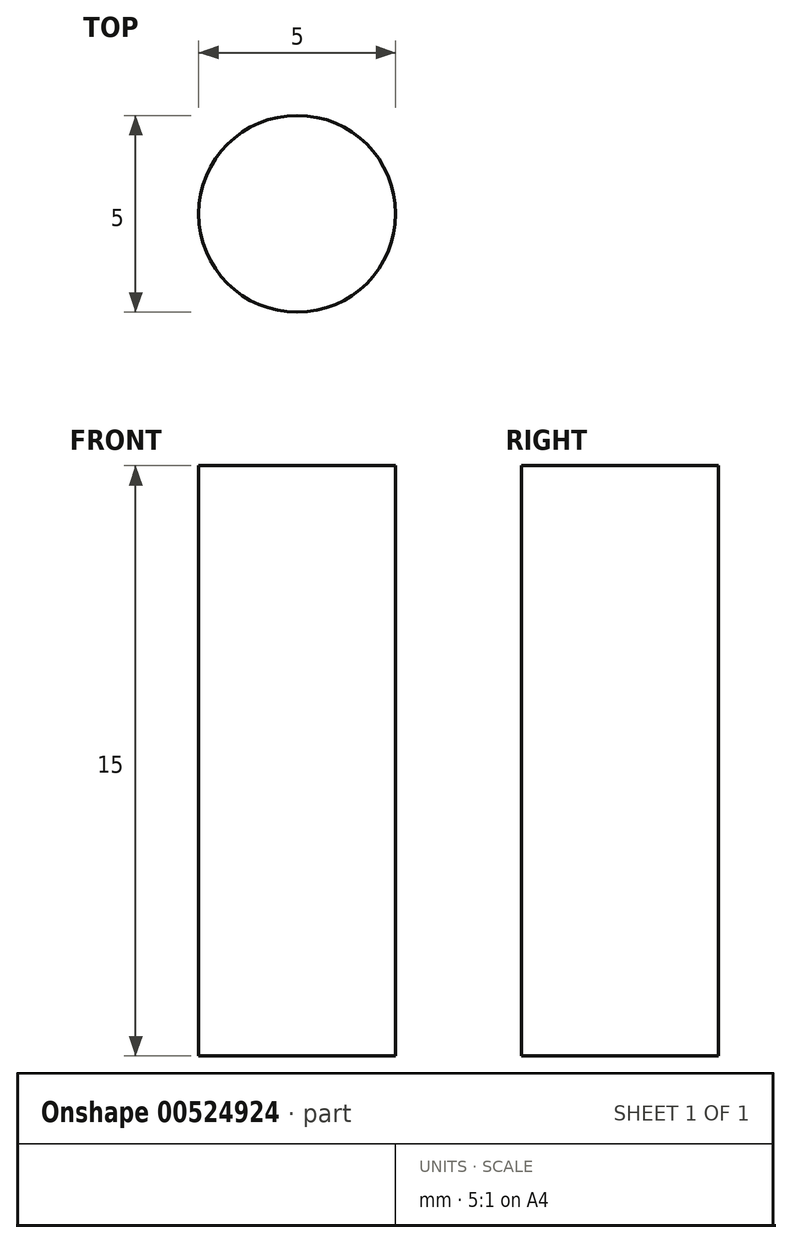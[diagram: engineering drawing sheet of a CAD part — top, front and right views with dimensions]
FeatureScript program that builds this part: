
annotation { "Feature Type Name" : "Feature", "Feature Type Description" : "" }
export const myFeature = defineFeature(function(context is Context, id is Id, definition is map)
    precondition{}
    {
        {
            var Q0;
            Q0=qCreatedBy(makeId("Top.planeOp"),FACE);
            var sketch = newSketch(context, id + "F0", { "sketchPlane" : qUnion([Q0])});
            skCircle(sketch, "E0", {"center": v(0, 0) * mm, "radius": 2.5 * mm});
            skSolve(sketch);
        }
        {
            var Q0;
            Q0 = qSketchRegion(id + "F0", true);
            extrude(context, id + "F1", {"entities" : qUnion([Q0]), "depth" : 15 * mm, "offsetDistance" : 25 * mm});
        }
    });
